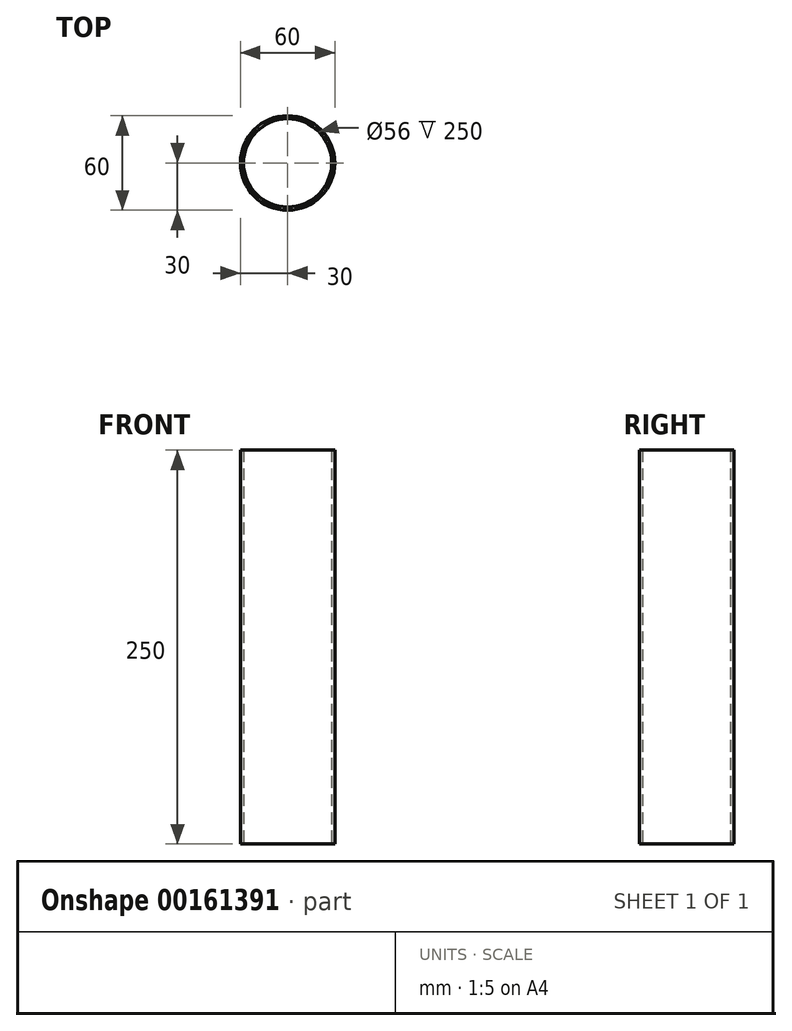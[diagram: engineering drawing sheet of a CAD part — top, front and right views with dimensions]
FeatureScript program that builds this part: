
annotation { "Feature Type Name" : "Feature", "Feature Type Description" : "" }
export const myFeature = defineFeature(function(context is Context, id is Id, definition is map)
    precondition{}
    {
        {
            var Q0;
            Q0=qCreatedBy(makeId("Top.planeOp"),FACE);
            var sketch = newSketch(context, id + "F0", { "sketchPlane" : qUnion([Q0])});
            skCircle(sketch, "E0", {"center": v(0, 0) * mm, "radius": 30 * mm});
            skCircle(sketch, "E1.0", {"center": v(0, 0) * mm, "radius": 28 * mm});
            skSolve(sketch);
        }
        {
            var Q0;
            Q0=makeQuery(id+"F0.imprint","IMPRINT",FACE,{"disambiguationData":[TD([[makeQuery(id+"F0.imprint","IMPRINT",EDGE,{"derivedFrom":sQuery(id+"F0.wireOp",EDGE,"E0")}),1.0]])]});
            extrude(context, id + "F1", {"entities" : qUnion([Q0]), "depth" : 250 * mm});
        }
    });
